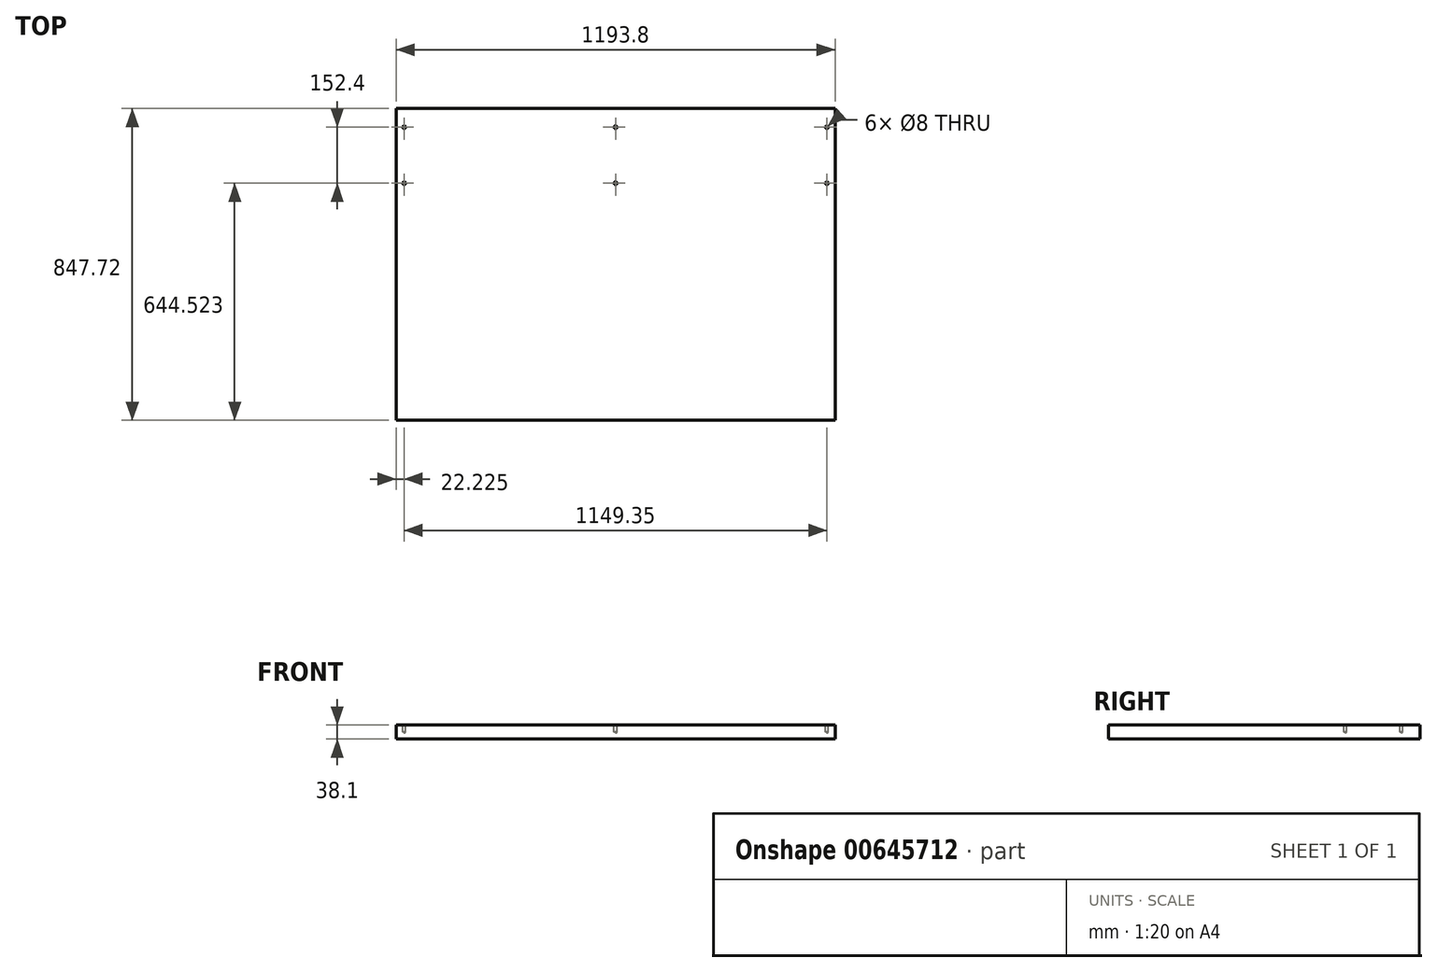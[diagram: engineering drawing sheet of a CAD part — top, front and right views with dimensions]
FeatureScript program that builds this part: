
annotation { "Feature Type Name" : "Feature", "Feature Type Description" : "" }
export const myFeature = defineFeature(function(context is Context, id is Id, definition is map)
    precondition{}
    {
        {
            var Q0;
            Q0=qCreatedBy(makeId("Top.planeOp"),FACE);
            var sketch = newSketch(context, id + "F0", { "sketchPlane" : qUnion([Q0])});
            skLineSegment(sketch, "E0.bottom", {"start": v(-596.9, 423.86) * mm, "end": v(596.9, 423.86) * mm});
            skLineSegment(sketch, "E0.top", {"start": v(-596.9, -423.86) * mm, "end": v(596.9, -423.86) * mm});
            skLineSegment(sketch, "E0.left", {"start": v(-596.9, 423.86) * mm, "end": v(-596.9, -423.86) * mm});
            skLineSegment(sketch, "E0.right", {"start": v(596.9, 423.86) * mm, "end": v(596.9, -423.86) * mm});
            skPoint(sketch, "E0.middle", {"position": v(0, 0) * mm});
            skSolve(sketch);
        }
        {
            var Q0;
            Q0=makeQuery(id+"F0.imprint","IMPRINT",FACE,{"disambiguationData":[TD([[makeQuery(id+"F0.imprint","IMPRINT",EDGE,{"derivedFrom":sQuery(id+"F0.wireOp",EDGE,"E0.bottom")}),-1.0]])]});
            extrude(context, id + "F1", {"entities" : qUnion([Q0]), "depth" : 38.1 * mm, "offsetDistance" : 25.4 * mm});
        }
        {
            var Q0;
            Q0=makeQuery(id+"F1.opExtrude","CAP_FACE",FACE,{"disambiguationData":[OSD([sQuery(id+"F0.wireOp",EDGE,"E0.bottom"),sQuery(id+"F0.wireOp",EDGE,"E0.top"),sQuery(id+"F0.wireOp",EDGE,"E0.left"),sQuery(id+"F0.wireOp",EDGE,"E0.right")])],"isStart":false});
            var sketch = newSketch(context, id + "F2", { "sketchPlane" : qUnion([Q0])});
            skLineSegment(sketch, "E1", {"start": v(0, 423.86) * mm, "end": v(-574.68, 423.86) * mm});
            skLineSegment(sketch, "E2", {"start": v(0, 423.86) * mm, "end": v(574.68, 423.86) * mm});
            skLineSegment(sketch, "E3", {"start": v(0, 423.86) * mm, "end": v(0, 373.06) * mm});
            skLineSegment(sketch, "E4", {"start": v(-574.68, 423.86) * mm, "end": v(-574.68, 373.06) * mm});
            skLineSegment(sketch, "E5", {"start": v(574.68, 423.86) * mm, "end": v(574.68, 373.06) * mm});
            skLineSegment(sketch, "E6", {"start": v(-574.68, 373.06) * mm, "end": v(-574.68, 220.66) * mm});
            skLineSegment(sketch, "E7", {"start": v(574.68, 373.06) * mm, "end": v(574.68, 220.66) * mm});
            skLineSegment(sketch, "E8", {"start": v(0, 373.06) * mm, "end": v(0, 220.66) * mm});
            skPoint(sketch, "E9", {"position": v(-574.68, 373.06) * mm});
            skPoint(sketch, "E10", {"position": v(-574.68, 220.66) * mm});
            skPoint(sketch, "E11", {"position": v(0, 373.06) * mm});
            skPoint(sketch, "E12", {"position": v(0, 220.66) * mm});
            skPoint(sketch, "E13", {"position": v(574.68, 373.06) * mm});
            skPoint(sketch, "E14", {"position": v(574.68, 220.66) * mm});
            skSolve(sketch);
        }
        {
            var Q0;
            Q0=sQuery(id+"F2.wireOp",VERTEX,"E9");
            var Q1;
            Q1=sQuery(id+"F2.wireOp",VERTEX,"E10");
            var Q2;
            Q2=sQuery(id+"F2.wireOp",VERTEX,"E11");
            var Q3;
            Q3=sQuery(id+"F2.wireOp",VERTEX,"E12");
            var Q4;
            Q4=sQuery(id+"F2.wireOp",VERTEX,"E13");
            var Q5;
            Q5=sQuery(id+"F2.wireOp",VERTEX,"E14");
            var Q6;
            Q6=makeQuery(id+"F1.opExtrude","SWEPT_BODY",BODY,{"disambiguationData":[OSD([sQuery(id+"F0.wireOp",EDGE,"E0.bottom"),sQuery(id+"F0.wireOp",EDGE,"E0.top"),sQuery(id+"F0.wireOp",EDGE,"E0.left"),sQuery(id+"F0.wireOp",EDGE,"E0.right")])]});
            hole(context, id + "F3", {"style" : HoleStyle.SIMPLE, "endStyle" : HoleEndStyle.BLIND, "holeDiameter" : 8 * mm, "majorDiameter" : 6.35 * mm, "holeDepth" : 19.05 * mm, "isTappedThrough" : true, "tappedDepth" : 12.7 * mm, "tapClearance" : 3, "startFromSketch" : true, "locations" : qUnion([Q0, Q1, Q2, Q3, Q4, Q5]), "scope" : qUnion([Q6])});
        }
    });
